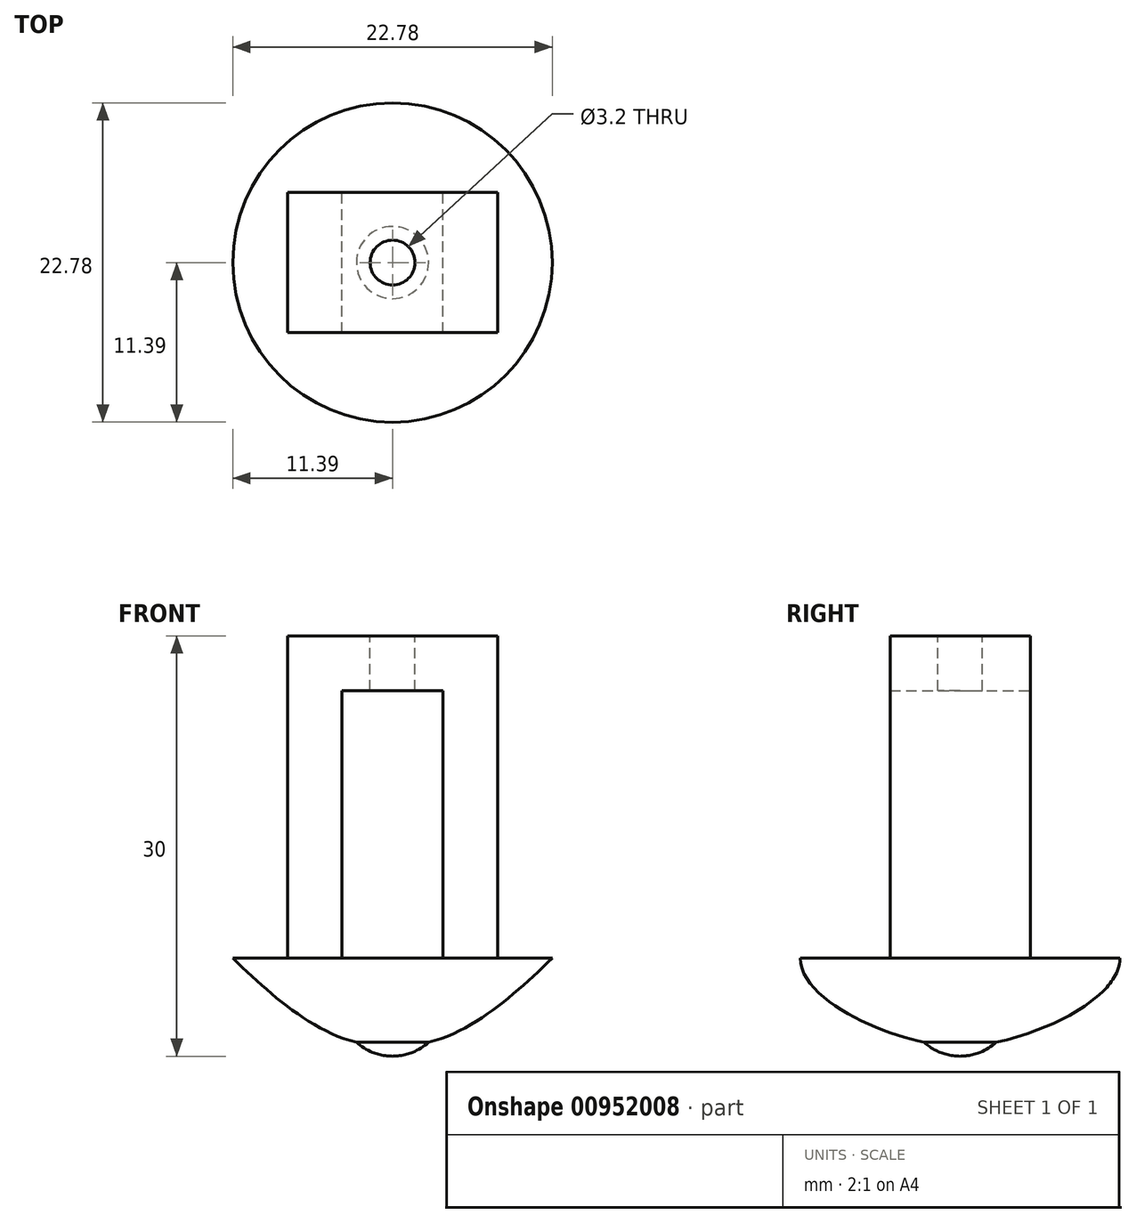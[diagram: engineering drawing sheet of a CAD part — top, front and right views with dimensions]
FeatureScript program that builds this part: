
annotation { "Feature Type Name" : "Feature", "Feature Type Description" : "" }
export const myFeature = defineFeature(function(context is Context, id is Id, definition is map)
    precondition{}
    {
        {
            var Q0;
            Q0=qCreatedBy(makeId("Front.planeOp"),FACE);
            var sketch = newSketch(context, id + "F0", { "sketchPlane" : qUnion([Q0])});
            skLineSegment(sketch, "E0.bottom", {"start": v(7.5, 11.5) * mm, "end": v(-7.5, 11.5) * mm});
            skLineSegment(sketch, "E0.top", {"start": v(7.5, -11.5) * mm, "end": v(-7.5, -11.5) * mm});
            skLineSegment(sketch, "E0.left", {"start": v(7.5, 11.5) * mm, "end": v(7.5, -11.5) * mm});
            skLineSegment(sketch, "E0.right", {"start": v(-7.5, 11.5) * mm, "end": v(-7.5, -11.5) * mm});
            skPoint(sketch, "E0.middle", {"position": v(0, 0) * mm});
            skLineSegment(sketch, "E1.0", {"start": v(3.6, 7.6) * mm, "end": v(-3.6, 7.6) * mm});
            skLineSegment(sketch, "E1.1", {"start": v(3.6, 7.6) * mm, "end": v(3.6, -11.5) * mm});
            skLineSegment(sketch, "E1.3", {"start": v(-3.6, 7.6) * mm, "end": v(-3.6, -11.5) * mm});
            skLineSegment(sketch, "E2", {"start": v(-17.68, -19.5) * mm, "end": v(29.9, -19.5) * mm, "construction": true});
            skSolve(sketch);
        }
        {
            var Q0;
            Q0=makeQuery(id+"F0.imprint","IMPRINT",FACE,{"disambiguationData":[TD([[makeQuery(id+"F0.imprint","IMPRINT",EDGE,{"derivedFrom":sQuery(id+"F0.wireOp",EDGE,"E0.bottom")}),1.0]])]});
            extrude(context, id + "F1", {"entities" : qUnion([Q0]), "depth" : 10 * mm, "offsetDistance" : 25 * mm});
        }
        {
            var Q0;
            Q0=makeQuery(id+"F1.opExtrude","SWEPT_FACE",FACE,{"disambiguationData":[OSD([sQuery(id+"F0.wireOp",EDGE,"E0.bottom")])]});
            var sketch = newSketch(context, id + "F2", { "sketchPlane" : qUnion([Q0])});
            skPoint(sketch, "E3", {"position": v(0, 0) * mm});
            skPoint(sketch, "E4", {"position": v(7.5, -5) * mm});
            skCircle(sketch, "E5", {"center": v(0, -5) * mm, "radius": 1.6 * mm});
            skSolve(sketch);
        }
        {
            var Q0;
            Q0 = qSketchRegion(id + "F2", true);
            extrude(context, id + "F3", {"entities" : qUnion([Q0]), "operationType" : NewBodyOperationType.REMOVE, "oppositeDirection" : true, "depth" : 4.7 * mm, "offsetDistance" : 25 * mm});
        }
        {
            var Q0;
            Q0=makeQuery(id+"F1.opExtrude","CAP_VERTEX",VERTEX,{"disambiguationData":[OSD([sQuery(id+"F0.wireOp",EDGE,"E0.top"),sQuery(id+"F0.wireOp",EDGE,"E0.right")])],"isStart":false});
            var Q1;
            Q1=makeQuery(id+"F1.opExtrude","CAP_VERTEX",VERTEX,{"disambiguationData":[OSD([sQuery(id+"F0.wireOp",EDGE,"E0.top"),sQuery(id+"F0.wireOp",EDGE,"E1.3")])],"isStart":false});
            var Q2;
            Q2=makeQuery(id+"F1.opExtrude","CAP_VERTEX",VERTEX,{"disambiguationData":[OSD([sQuery(id+"F0.wireOp",EDGE,"E0.top"),sQuery(id+"F0.wireOp",EDGE,"E0.right")])],"isStart":true});
            cPlane(context, id + "F4", {"entities" : qUnion([Q0, Q1, Q2]), "cplaneType" : CPlaneType.THREE_POINT, "offset" : 25 * mm, "width" : 150 * mm, "height" : 150 * mm});
        }
        {
            var Q0;
            Q0=qCreatedBy(id+"F4.planeOp",FACE);
            var sketch = newSketch(context, id + "F5", { "sketchPlane" : qUnion([Q0])});
            skPoint(sketch, "E6.0", {"position": v(0, 5) * mm});
            skCircle(sketch, "E7", {"center": v(0, 5) * mm, "radius": 11.4 * mm});
            skSolve(sketch);
        }
        {
            var Q0;
            Q0=makeQuery(id+"F5.imprint","IMPRINT",FACE,{"disambiguationData":[TD([[makeQuery(id+"F5.imprint","IMPRINT",EDGE,{"derivedFrom":sQuery(id+"F5.wireOp",EDGE,"E7")}),1.0]])]});
            cPlane(context, id + "F6", {"entities" : qUnion([Q0]), "cplaneType" : CPlaneType.OFFSET, "offset" : 6 * mm, "width" : 150 * mm, "height" : 150 * mm});
        }
        {
            var Q0;
            Q0=qCreatedBy(id+"F6.planeOp",FACE);
            var sketch = newSketch(context, id + "F7", { "sketchPlane" : qUnion([Q0])});
            skPoint(sketch, "E8.0", {"position": v(0, 5) * mm});
            skCircle(sketch, "E9", {"center": v(0, 5) * mm, "radius": 2.57 * mm});
            skSolve(sketch);
        }
        {
            var Q0;
            Q0=qCreatedBy(id+"F6.planeOp",FACE);
            cPlane(context, id + "F8", {"entities" : qUnion([Q0]), "cplaneType" : CPlaneType.OFFSET, "offset" : 1 * mm, "width" : 150 * mm, "height" : 150 * mm});
        }
        {
            var Q0;
            Q0=qCreatedBy(makeId("Right.planeOp"),FACE);
            var sketch = newSketch(context, id + "F9", { "sketchPlane" : qUnion([Q0])});
            skLineSegment(sketch, "E10.0", {"start": v(6.4, -11.5) * mm, "end": v(-16.4, -11.5) * mm});
            skLineSegment(sketch, "E11.0", {"start": v(-2.43, -17.5) * mm, "end": v(-7.57, -17.5) * mm});
            skFitSpline(sketch, "E12", {"points": [v(-16.4, -11.5) * mm, v(-7.57, -17.5) * mm], "startDerivative": vector(0.02, -8.62) * mm, "endDerivative": vector(10.12, -2.05) * mm});
            skLineSegment(sketch, "E13", {"start": v(-5, -11.5) * mm, "end": v(-5, -17.5) * mm, "construction": true});
            skFitSpline(sketch, "E14.MirrorCS", {"points": [v(6.4, -11.5) * mm, v(-2.43, -17.5) * mm], "startDerivative": vector(-0.02, -8.62) * mm, "endDerivative": vector(-10.12, -2.05) * mm});
            skSolve(sketch);
        }
        {
            var Q1;
            Q1=makeQuery(id+"F5.imprint","IMPRINT",FACE,{"disambiguationData":[TD([[makeQuery(id+"F5.imprint","IMPRINT",EDGE,{"derivedFrom":sQuery(id+"F5.wireOp",EDGE,"E7")}),1.0]])]});
            var Q2;
            Q2=makeQuery(id+"F7.imprint","IMPRINT",FACE,{"disambiguationData":[TD([[makeQuery(id+"F7.imprint","IMPRINT",EDGE,{"derivedFrom":sQuery(id+"F7.wireOp",EDGE,"E9")}),1.0]])]});
            var Q3;
            Q3=sQuery(id+"F9.wireOp",EDGE,"E12");
            var Q4;
            Q4=sQuery(id+"F9.wireOp",EDGE,"E14.MirrorCS");
            loft(context, id + "F10", {"operationType" : NewBodyOperationType.ADD, "addGuides" : true, "sheetProfilesArray" : [{ "sheetProfileEntities" : qUnion([Q1]) }, { "sheetProfileEntities" : qUnion([Q2]) }], "guidesArray" : [{ "guideEntities" : qUnion([Q3]), "guideDerivativeType" : LoftGuideDerivativeType.DEFAULT, "guideDerivativeMagnitude" : 1 }, { "guideEntities" : qUnion([Q4]), "guideDerivativeType" : LoftGuideDerivativeType.DEFAULT, "guideDerivativeMagnitude" : 1 }]});
        }
        {
            var Q0;
            Q0=qCreatedBy(id+"F8.planeOp",FACE);
            var sketch = newSketch(context, id + "F11", { "sketchPlane" : qUnion([Q0])});
            skPoint(sketch, "E15.0", {"position": v(0, 5) * mm});
            skSolve(sketch);
        }
        {
            var Q0;
            Q0=qCreatedBy(makeId("Right.planeOp"),FACE);
            var sketch = newSketch(context, id + "F12", { "sketchPlane" : qUnion([Q0])});
            skPoint(sketch, "E16.0", {"position": v(-5, -18.5) * mm});
            skFitSpline(sketch, "E17.0", {"points": [v(-2.43, -17.5) * mm, v(-4.14, -17.5) * mm, v(-5.86, -17.5) * mm, v(-7.57, -17.5) * mm]});
            skLineSegment(sketch, "E18", {"start": v(-5, -18.5) * mm, "end": v(-5, -17.5) * mm});
            skFitSpline(sketch, "E19", {"points": [v(-7.57, -17.5) * mm, v(-5, -18.5) * mm], "startDerivative": vector(2.45, -2.12) * mm, "endDerivative": vector(3.12, -0.15) * mm});
            skSolve(sketch);
        }
        {
            var Q0;
            {var subQ2=sQuery(id+"F12.wireOp",EDGE,"E18");Q0=makeQuery(id+"F12.imprint","IMPRINT",FACE,{"disambiguationData":[TD([[makeQuery(id+"F12.imprint","IMPRINT",EDGE,{"derivedFrom":subQ2}),1.0]])]});}
            var Q1;
            Q1=sQuery(id+"F12.wireOp",EDGE,"E18");
            revolve(context, id + "F13", {"operationType" : NewBodyOperationType.ADD, "surfaceOperationType" : NewSurfaceOperationType.NEW, "entities" : qUnion([Q0]), "axis" : qUnion([Q1]), "revolveType" : RevolveType.FULL});
        }
    });
